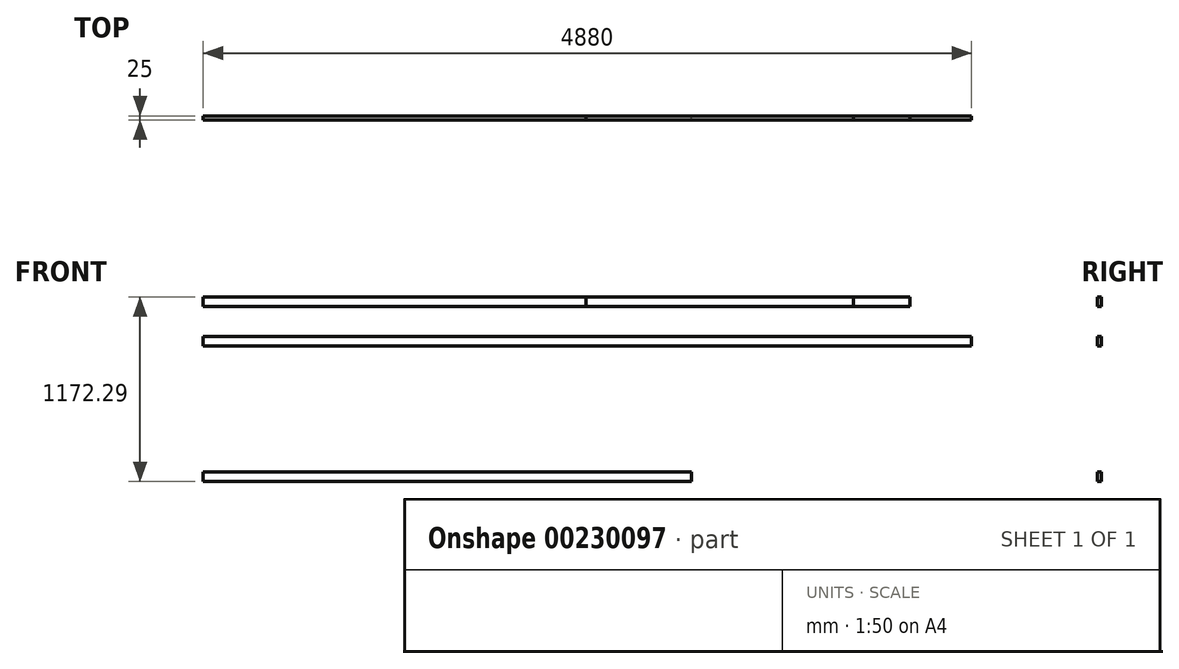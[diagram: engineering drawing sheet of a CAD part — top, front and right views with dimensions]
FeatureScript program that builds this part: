
annotation { "Feature Type Name" : "Feature", "Feature Type Description" : "" }
export const myFeature = defineFeature(function(context is Context, id is Id, definition is map)
    precondition{}
    {
        {
            var Q0;
            Q0=qCreatedBy(makeId("Front.planeOp"),FACE);
            var sketch = newSketch(context, id + "F0", { "sketchPlane" : qUnion([Q0])});
            skLineSegment(sketch, "E0.bottom", {"start": v(-2440, 0) * mm, "end": v(2440, 0) * mm});
            skLineSegment(sketch, "E0.top", {"start": v(-2440, -60) * mm, "end": v(2440, -60) * mm});
            skLineSegment(sketch, "E0.left", {"start": v(-2440, 0) * mm, "end": v(-2440, -60) * mm});
            skLineSegment(sketch, "E0.right", {"start": v(2440, 0) * mm, "end": v(2440, -60) * mm});
            skPoint(sketch, "E1", {"position": v(0, 0) * mm});
            skLineSegment(sketch, "E2", {"start": v(-2440, 0) * mm, "end": v(-2440, -2135.36) * mm, "construction": true});
            skLineSegment(sketch, "E3.bottom", {"start": v(-2440, -508.84) * mm, "end": v(-10, -508.84) * mm});
            skLineSegment(sketch, "E3.top", {"start": v(-2440, -568.84) * mm, "end": v(-10, -568.84) * mm});
            skLineSegment(sketch, "E3.left", {"start": v(-2440, -508.84) * mm, "end": v(-2440, -568.84) * mm});
            skLineSegment(sketch, "E3.right", {"start": v(-10, -508.84) * mm, "end": v(-10, -568.84) * mm});
            skLineSegment(sketch, "E4.bottom", {"start": v(-2440, -758.52) * mm, "end": v(4140, -758.52) * mm});
            skLineSegment(sketch, "E4.top", {"start": v(-2440, -818.52) * mm, "end": v(4140, -818.52) * mm});
            skLineSegment(sketch, "E4.left", {"start": v(-2440, -758.52) * mm, "end": v(-2440, -818.52) * mm});
            skLineSegment(sketch, "E4.right", {"start": v(4140, -758.52) * mm, "end": v(4140, -818.52) * mm});
            skLineSegment(sketch, "E5.bottom", {"start": v(-2440, -989.73) * mm, "end": v(-2080, -989.73) * mm});
            skLineSegment(sketch, "E5.top", {"start": v(-2440, -1049.73) * mm, "end": v(-2080, -1049.73) * mm});
            skLineSegment(sketch, "E5.left", {"start": v(-2440, -989.73) * mm, "end": v(-2440, -1049.73) * mm});
            skLineSegment(sketch, "E5.right", {"start": v(-2080, -989.73) * mm, "end": v(-2080, -1049.73) * mm});
            skLineSegment(sketch, "E6.bottom", {"start": v(-2440, -1621.13) * mm, "end": v(660, -1621.13) * mm});
            skLineSegment(sketch, "E6.top", {"start": v(-2440, -1681.13) * mm, "end": v(660, -1681.13) * mm});
            skLineSegment(sketch, "E6.left", {"start": v(-2440, -1621.13) * mm, "end": v(-2440, -1681.13) * mm});
            skLineSegment(sketch, "E6.right", {"start": v(660, -1621.13) * mm, "end": v(660, -1681.13) * mm});
            skLineSegment(sketch, "E7", {"start": v(660, -1621.13) * mm, "end": v(660, 719.97) * mm, "construction": true});
            skLineSegment(sketch, "E8", {"start": v(2440, -60) * mm, "end": v(2440, -1028.21) * mm, "construction": true});
            skLineSegment(sketch, "E9.bottom", {"start": v(-10, -508.84) * mm, "end": v(1690, -508.84) * mm});
            skLineSegment(sketch, "E9.top", {"start": v(-10, -568.84) * mm, "end": v(1690, -568.84) * mm});
            skLineSegment(sketch, "E9.right", {"start": v(1690, -508.84) * mm, "end": v(1690, -568.84) * mm});
            skLineSegment(sketch, "E10.bottom", {"start": v(1690, -508.84) * mm, "end": v(2050, -508.84) * mm});
            skLineSegment(sketch, "E10.top", {"start": v(1690, -568.84) * mm, "end": v(2050, -568.84) * mm});
            skLineSegment(sketch, "E10.right", {"start": v(2050, -508.84) * mm, "end": v(2050, -568.84) * mm});
            skLineSegment(sketch, "E11", {"start": v(2440, -758.52) * mm, "end": v(2440, -818.52) * mm});
            skSolve(sketch);
        }
        {
            var Q0;
            Q0=makeQuery(id+"F0.imprint","IMPRINT",FACE,{"disambiguationData":[TD([[makeQuery(id+"F0.imprint","IMPRINT",EDGE,{"derivedFrom":sQuery(id+"F0.wireOp",EDGE,"E3.bottom")}),-1.0]])]});
            var Q1;
            Q1=makeQuery(id+"F0.imprint","IMPRINT",FACE,{"disambiguationData":[TD([[makeQuery(id+"F0.imprint","IMPRINT",EDGE,{"derivedFrom":sQuery(id+"F0.wireOp",EDGE,"E10.bottom")}),-1.0]])]});
            var Q2;
            Q2=makeQuery(id+"F0.imprint","IMPRINT",FACE,{"disambiguationData":[TD([[makeQuery(id+"F0.imprint","IMPRINT",EDGE,{"derivedFrom":sQuery(id+"F0.wireOp",EDGE,"E6.bottom")}),-1.0]])]});
            extrude(context, id + "F1", {"entities" : qUnion([Q0, Q1, Q2]), "depth" : 25 * mm, "offsetDistance" : 25 * mm});
        }
        {
            var Q0;
            Q0=makeQuery(id+"F0.imprint","IMPRINT",FACE,{"disambiguationData":[TD([[makeQuery(id+"F0.imprint","IMPRINT",EDGE,{"derivedFrom":sQuery(id+"F0.wireOp",EDGE,"E9.bottom")}),-1.0]])]});
            var Q1;
            {var subQ0=sQuery(id+"F0.wireOp",EDGE,"E4.left");Q1=makeQuery(id+"F0.imprint","IMPRINT",FACE,{"disambiguationData":[TD([[makeQuery(id+"F0.imprint","IMPRINT",EDGE,{"derivedFrom":subQ0}),1.0]])]});}
            extrude(context, id + "F2", {"entities" : qUnion([Q0, Q1]), "depth" : 25 * mm, "offsetDistance" : 25 * mm});
        }
    });
